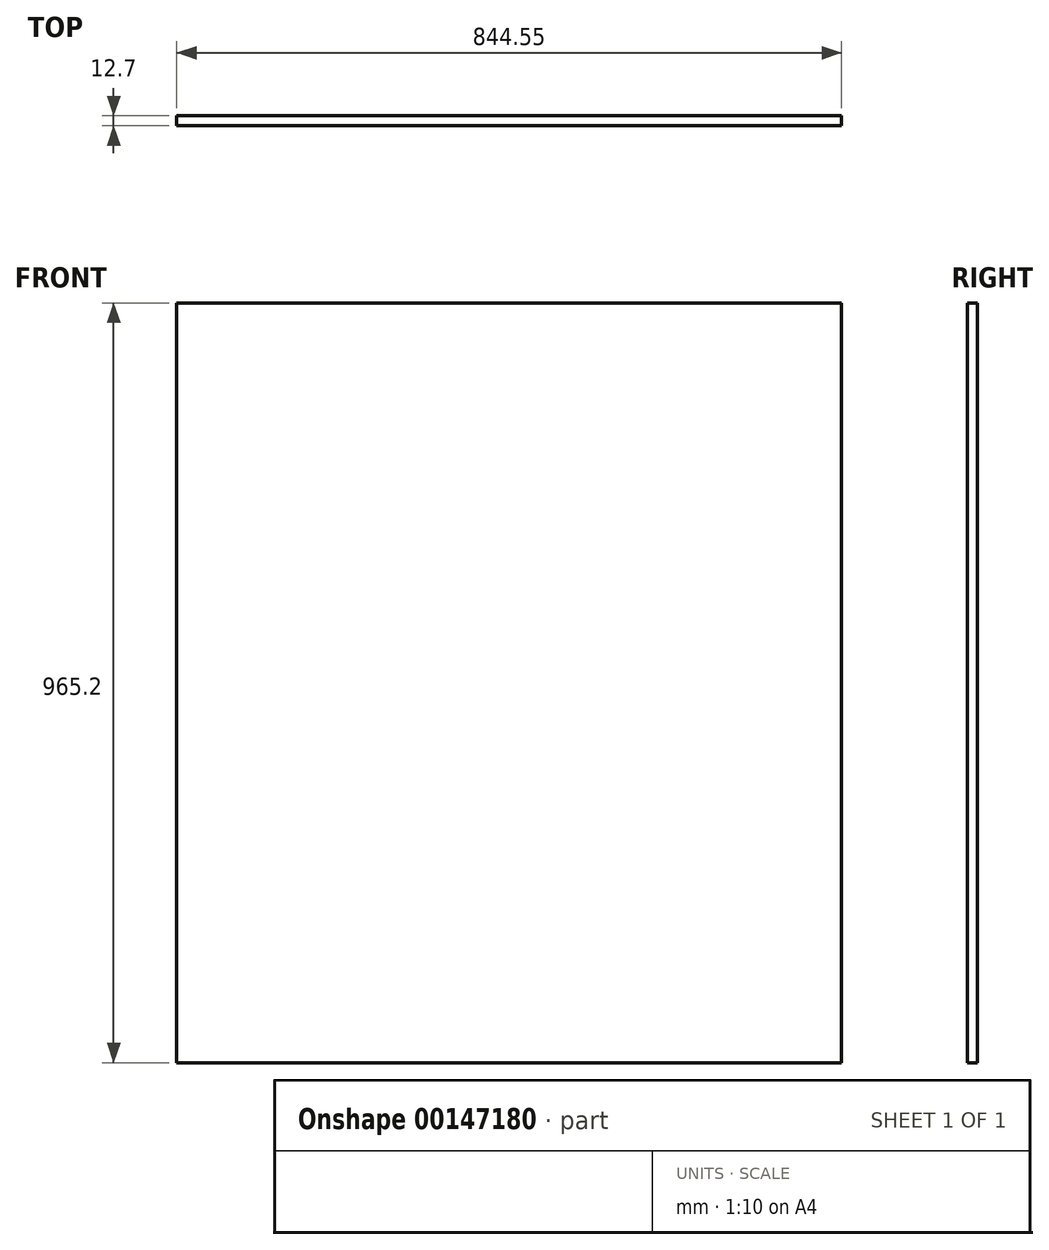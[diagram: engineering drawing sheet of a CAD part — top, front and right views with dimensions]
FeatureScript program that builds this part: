
annotation { "Feature Type Name" : "Feature", "Feature Type Description" : "" }
export const myFeature = defineFeature(function(context is Context, id is Id, definition is map)
    precondition{}
    {
        {
            var Q0;
            Q0=qCreatedBy(makeId("Front.planeOp"),FACE);
            var sketch = newSketch(context, id + "F0", { "sketchPlane" : qUnion([Q0])});
            skLineSegment(sketch, "E0.bottom", {"start": v(0, 0) * mm, "end": v(844.55, 0) * mm});
            skLineSegment(sketch, "E0.top", {"start": v(0, 965.2) * mm, "end": v(844.55, 965.2) * mm});
            skLineSegment(sketch, "E0.left", {"start": v(0, 0) * mm, "end": v(0, 965.2) * mm});
            skLineSegment(sketch, "E0.right", {"start": v(844.55, 0) * mm, "end": v(844.55, 965.2) * mm});
            skSolve(sketch);
        }
        {
            var Q0;
            Q0=makeQuery(id+"F0.imprint","IMPRINT",FACE,{"disambiguationData":[TD([[makeQuery(id+"F0.imprint","IMPRINT",EDGE,{"derivedFrom":sQuery(id+"F0.wireOp",EDGE,"E0.bottom")}),1.0]])]});
            extrude(context, id + "F1", {"entities" : qUnion([Q0]), "depth" : 12.7 * mm});
        }
    });
